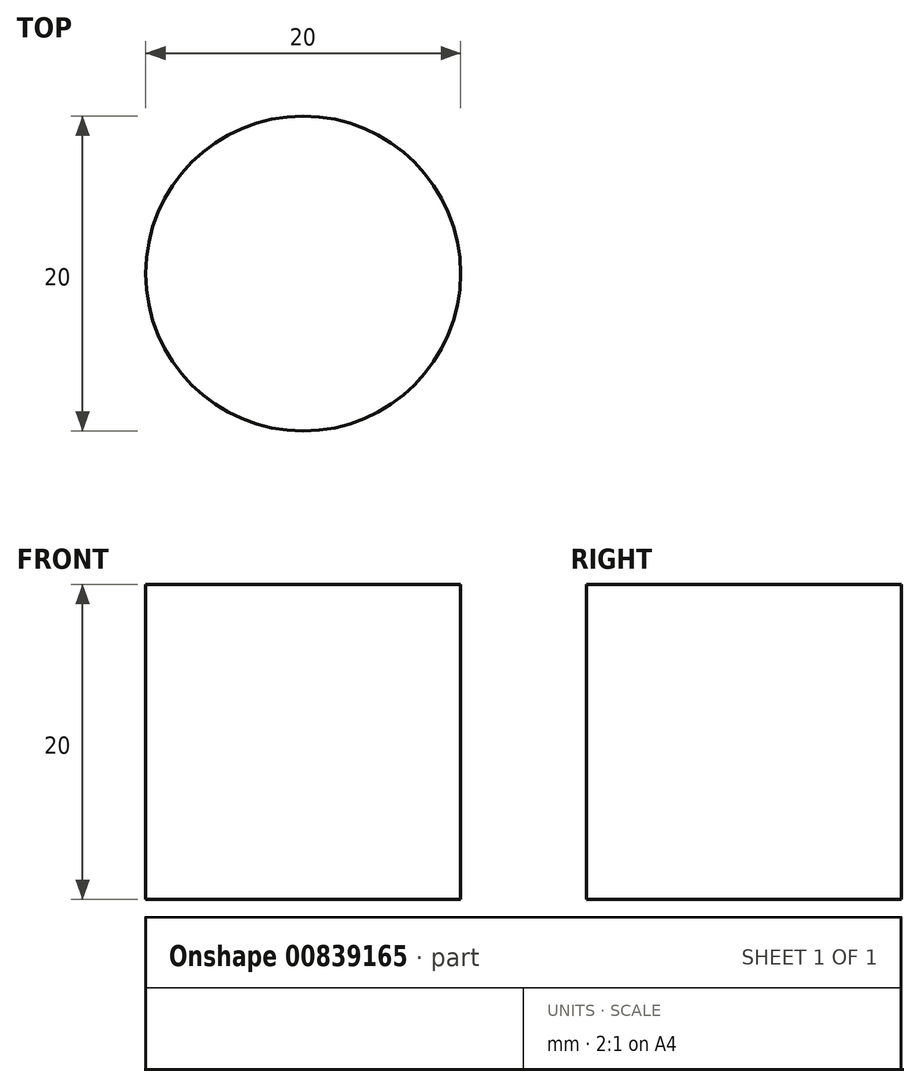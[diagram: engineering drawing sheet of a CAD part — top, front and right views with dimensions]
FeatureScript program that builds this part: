
annotation { "Feature Type Name" : "Feature", "Feature Type Description" : "" }
export const myFeature = defineFeature(function(context is Context, id is Id, definition is map)
    precondition{}
    {
        {
            var Q0;
            Q0=qCreatedBy(makeId("Top.planeOp"),FACE);
            var sketch = newSketch(context, id + "F0", { "sketchPlane" : qUnion([Q0])});
            skCircle(sketch, "E0", {"center": v(0, 0) * mm, "radius": 10 * mm});
            skSolve(sketch);
        }
        {
            var Q0;
            Q0 = qSketchRegion(id + "F0", true);
            var sketch = newSketch(context, id + "F1", { "sketchPlane" : qUnion([Q0])});
            skSolve(sketch);
        }
        {
            var Q0;
            Q0=makeQuery(id+"F1.imprint","IMPRINT",FACE,{"disambiguationData":[TD([[makeQuery(id+"F1.imprint","IMPRINT",EDGE,{"derivedFrom":makeQuery(id+"F0.imprint","IMPRINT",EDGE,{"derivedFrom":sQuery(id+"F0.wireOp",EDGE,"E0")})}),1.0]])]});
            extrude(context, id + "F2", {"entities" : qUnion([Q0]), "depth" : 20 * mm, "offsetDistance" : 25.4 * mm});
        }
    });
